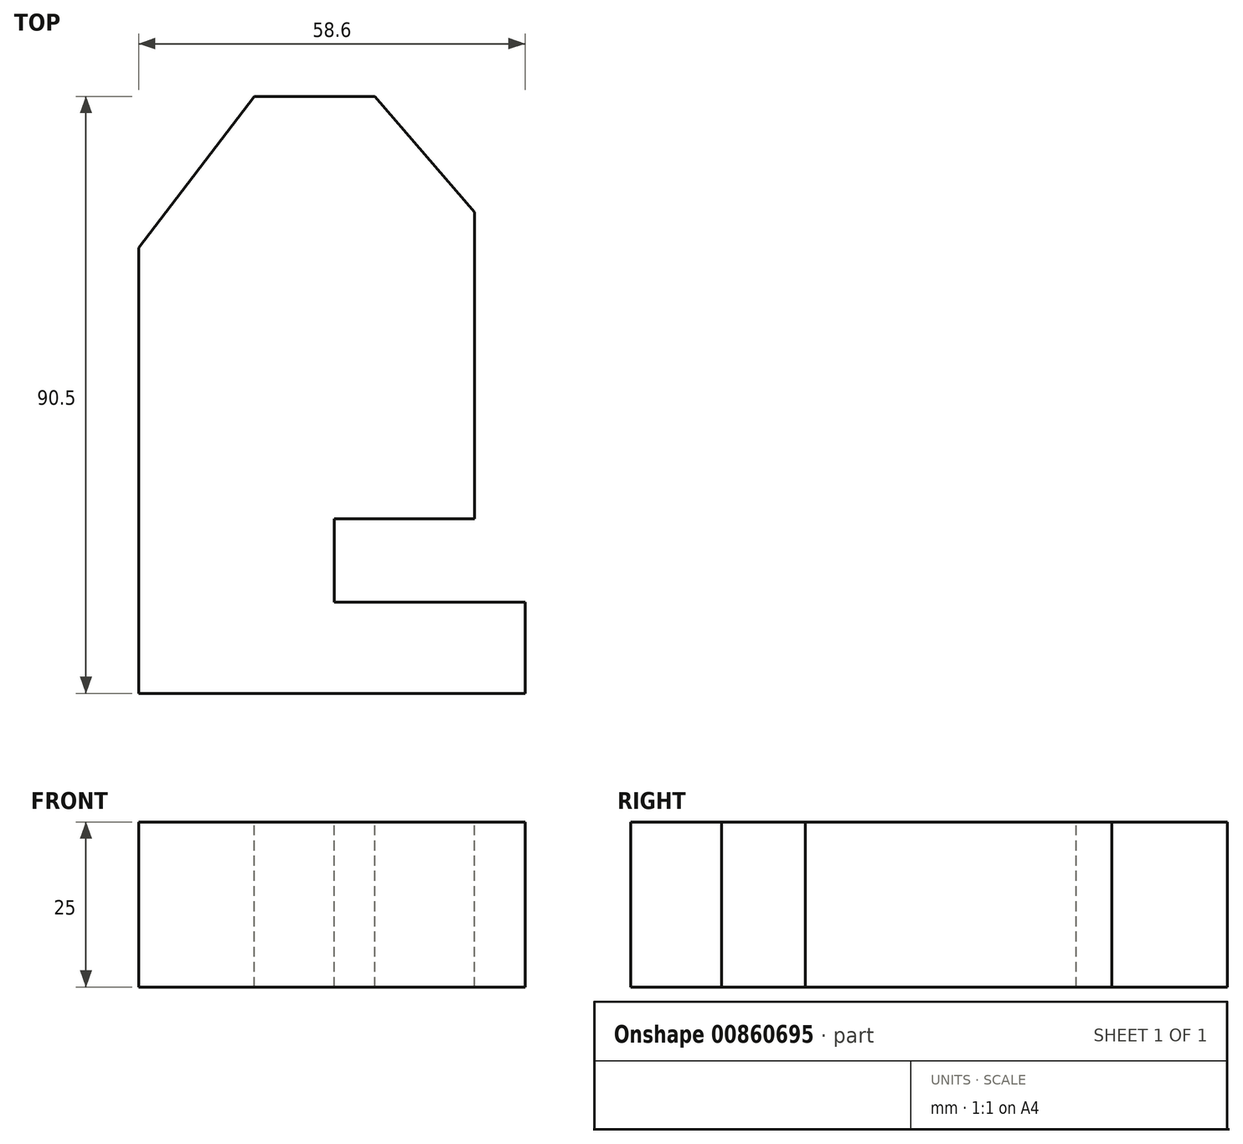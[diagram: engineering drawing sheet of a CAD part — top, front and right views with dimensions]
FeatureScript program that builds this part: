
annotation { "Feature Type Name" : "Feature", "Feature Type Description" : "" }
export const myFeature = defineFeature(function(context is Context, id is Id, definition is map)
    precondition{}
    {
        {
            var Q0;
            Q0=qCreatedBy(makeId("Top.planeOp"),FACE);
            var sketch = newSketch(context, id + "F0", { "sketchPlane" : qUnion([Q0])});
            skLineSegment(sketch, "E0.bottom", {"start": v(33.5, -45.25) * mm, "end": v(-33.5, -45.25) * mm});
            skLineSegment(sketch, "E0.top", {"start": v(33.5, 45.25) * mm, "end": v(-33.5, 45.25) * mm});
            skLineSegment(sketch, "E0.left", {"start": v(33.5, -45.25) * mm, "end": v(33.5, 45.25) * mm});
            skLineSegment(sketch, "E0.right", {"start": v(-33.5, -45.25) * mm, "end": v(-33.5, 45.25) * mm});
            skPoint(sketch, "E0.middle", {"position": v(0, 0) * mm});
            skSolve(sketch);
        }
        {
            var Q0;
            Q0=makeQuery(id+"F0.imprint","IMPRINT",FACE,{"disambiguationData":[TD([[makeQuery(id+"F0.imprint","IMPRINT",EDGE,{"derivedFrom":sQuery(id+"F0.wireOp",EDGE,"E0.bottom")}),-1.0]])]});
            extrude(context, id + "F1", {"entities" : qUnion([Q0]), "depth" : 25 * mm, "offsetDistance" : 25 * mm});
        }
        {
            var Q0;
            Q0=makeQuery(id+"F1.opExtrude","CAP_FACE",FACE,{"disambiguationData":[OSD([sQuery(id+"F0.wireOp",EDGE,"E0.bottom"),sQuery(id+"F0.wireOp",EDGE,"E0.top"),sQuery(id+"F0.wireOp",EDGE,"E0.left"),sQuery(id+"F0.wireOp",EDGE,"E0.right")])],"isStart":false});
            var sketch = newSketch(context, id + "F2", { "sketchPlane" : qUnion([Q0])});
            skLineSegment(sketch, "E1.bottom", {"start": v(33.5, -31.44) * mm, "end": v(17.45, -31.44) * mm});
            skLineSegment(sketch, "E1.top", {"start": v(33.5, 45.25) * mm, "end": v(17.45, 45.25) * mm});
            skLineSegment(sketch, "E1.left", {"start": v(33.5, -31.44) * mm, "end": v(33.5, 45.25) * mm});
            skLineSegment(sketch, "E1.right", {"start": v(17.45, -31.44) * mm, "end": v(17.45, 45.25) * mm});
            skSolve(sketch);
        }
        {
            var Q0;
            Q0=makeQuery(id+"F2.imprint","IMPRINT",FACE,{"disambiguationData":[TD([[makeQuery(id+"F2.imprint","IMPRINT",EDGE,{"derivedFrom":sQuery(id+"F2.wireOp",EDGE,"E1.bottom")}),-1.0]])]});
            extrude(context, id + "F3", {"entities" : qUnion([Q0]), "operationType" : NewBodyOperationType.REMOVE, "endBound" : BoundingType.THROUGH_ALL, "oppositeDirection" : true, "depth" : 25 * mm, "offsetDistance" : 25 * mm});
        }
        {
            var Q0;
            Q0=makeQuery(id+"F1.opExtrude","CAP_FACE",FACE,{"disambiguationData":[OSD([sQuery(id+"F0.wireOp",EDGE,"E0.bottom"),sQuery(id+"F0.wireOp",EDGE,"E0.top"),sQuery(id+"F0.wireOp",EDGE,"E0.left"),sQuery(id+"F0.wireOp",EDGE,"E0.right")])],"isStart":false});
            var sketch = newSketch(context, id + "F4", { "sketchPlane" : qUnion([Q0])});
            skLineSegment(sketch, "E2", {"start": v(2.33, 45.25) * mm, "end": v(17.45, 27.71) * mm});
            skLineSegment(sketch, "E3", {"start": v(-15.95, 45.25) * mm, "end": v(-33.5, 22.31) * mm});
            skSolve(sketch);
        }
        {
            var Q0;
            {var subQ0=sQuery(id+"F4.wireOp",EDGE,"E3");Q0=makeQuery(id+"F4.imprint","IMPRINT",FACE,{"disambiguationData":[TD([[makeQuery(id+"F4.imprint","IMPRINT",EDGE,{"derivedFrom":subQ0}),-1.0]])]});}
            var Q1;
            {var subQ0=sQuery(id+"F4.wireOp",EDGE,"E2");Q1=makeQuery(id+"F4.imprint","IMPRINT",FACE,{"disambiguationData":[TD([[makeQuery(id+"F4.imprint","IMPRINT",EDGE,{"derivedFrom":subQ0}),1.0]])]});}
            extrude(context, id + "F5", {"entities" : qUnion([Q0, Q1]), "operationType" : NewBodyOperationType.REMOVE, "endBound" : BoundingType.THROUGH_ALL, "oppositeDirection" : true, "depth" : 25 * mm, "offsetDistance" : 25 * mm});
        }
        {
            var Q0;
            Q0=makeQuery(id+"F1.opExtrude","CAP_FACE",FACE,{"disambiguationData":[OSD([sQuery(id+"F0.wireOp",EDGE,"E0.bottom"),sQuery(id+"F0.wireOp",EDGE,"E0.top"),sQuery(id+"F0.wireOp",EDGE,"E0.left"),sQuery(id+"F0.wireOp",EDGE,"E0.right")])],"isStart":false});
            var sketch = newSketch(context, id + "F6", { "sketchPlane" : qUnion([Q0])});
            skLineSegment(sketch, "E4.bottom", {"start": v(17.45, -31.44) * mm, "end": v(-3.83, -31.44) * mm});
            skLineSegment(sketch, "E4.top", {"start": v(17.45, -18.75) * mm, "end": v(-3.83, -18.75) * mm});
            skLineSegment(sketch, "E4.left", {"start": v(17.45, -31.44) * mm, "end": v(17.45, -18.75) * mm});
            skLineSegment(sketch, "E4.right", {"start": v(-3.83, -31.44) * mm, "end": v(-3.83, -18.75) * mm});
            skSolve(sketch);
        }
        {
            var Q0;
            Q0=makeQuery(id+"F6.imprint","IMPRINT",FACE,{"disambiguationData":[TD([[makeQuery(id+"F6.imprint","IMPRINT",EDGE,{"derivedFrom":sQuery(id+"F6.wireOp",EDGE,"E4.bottom")}),-1.0]])]});
            extrude(context, id + "F7", {"entities" : qUnion([Q0]), "operationType" : NewBodyOperationType.REMOVE, "endBound" : BoundingType.THROUGH_ALL, "oppositeDirection" : true, "depth" : 25 * mm, "offsetDistance" : 25 * mm});
        }
        {
            var Q0;
            Q0=makeQuery(id+"F1.opExtrude","CAP_FACE",FACE,{"disambiguationData":[OSD([sQuery(id+"F0.wireOp",EDGE,"E0.bottom"),sQuery(id+"F0.wireOp",EDGE,"E0.top"),sQuery(id+"F0.wireOp",EDGE,"E0.left"),sQuery(id+"F0.wireOp",EDGE,"E0.right")])],"isStart":false});
            var sketch = newSketch(context, id + "F8", { "sketchPlane" : qUnion([Q0])});
            skLineSegment(sketch, "E5", {"start": v(25.1, -31.44) * mm, "end": v(25.1, -45.25) * mm});
            skSolve(sketch);
        }
        {
            var Q0;
            {var subQ0=sQuery(id+"F8.wireOp",EDGE,"E5");Q0=makeQuery(id+"F8.imprint","IMPRINT",FACE,{"disambiguationData":[TD([[makeQuery(id+"F8.imprint","IMPRINT",EDGE,{"derivedFrom":subQ0}),1.0]])]});}
            extrude(context, id + "F9", {"entities" : qUnion([Q0]), "operationType" : NewBodyOperationType.REMOVE, "endBound" : BoundingType.THROUGH_ALL, "oppositeDirection" : true, "depth" : 25 * mm, "offsetDistance" : 25 * mm});
        }
    });
